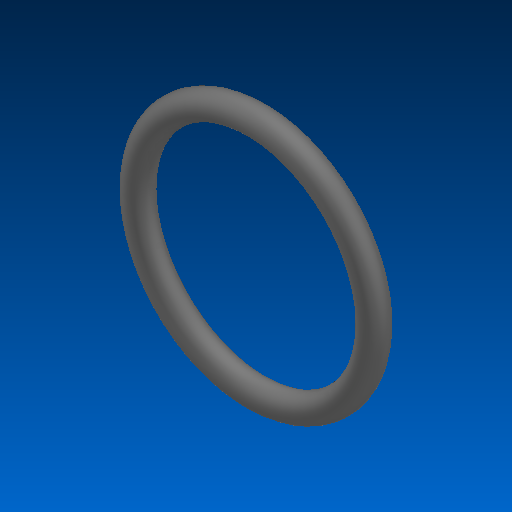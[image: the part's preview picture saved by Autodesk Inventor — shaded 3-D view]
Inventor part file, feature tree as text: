
AUTODESK INVENTOR PART (.ipt)
format: ipt  version: 2022.2 (Build 262287000, 287)  size: 135,168 bytes
history: native  units: in
note: dims shown in document units (in); Inventor stores cm internally (conversion verified against a paired STEP export)
features: revolve x1
ambient origin geometry x8: Origin, YZ Plane, XZ Plane, XY Plane, X Axis, Y Axis, Z Axis, Center Point
bodies: Solid1 (feature_tree)
feature tree (1):
  revolve  "Revolve1"  [1 undecoded]
note: 1 required parameter value undecoded (feature->parameter linkage not recoverable at this tier; creation-order binding heuristic only, values carry confidence <= 0.55)
